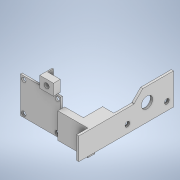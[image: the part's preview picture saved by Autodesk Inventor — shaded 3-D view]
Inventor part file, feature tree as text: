
AUTODESK INVENTOR PART (.ipt)
format: ipt  version: 2020.2 (Build 242310000, 310)  size: 344,576 bytes
history: native  units: mm
features: sketch x17, extrude x14, hole x4, projected_geometry x2
ambient origin geometry x8: Origin, YZ Plane, XZ Plane, XY Plane, X Axis, Y Axis, Z Axis, Center Point
bodies: Body1 (feature_tree)
feature tree (37):
  extrude  "Extrusion7"  Depth=6.08mm
  hole  "Hole4"  [1 undecoded]
  sketch  "Sketch16"  dims[d70=12.16mm d71=10.0mm]
  extrude  "Extrusion8"  Depth=10.0mm
  hole  "Hole5"  [1 undecoded]
  extrude  "Extrusion9"  Depth=32.05mm
  extrude  "Extrusion10"  Depth=32.05mm
  extrude  "Extrusion11"  Depth=3.0mm
  hole  "Hole6"  [1 undecoded]
  hole  "Hole7"  [1 undecoded]
  extrude  "Extrusion13"  Depth=26.05mm
  extrude  "Extrusion14"  Depth=4.0mm TaperAngle=0.0deg
  extrude  "Extrusion15"  Depth=10.0mm
  extrude  "Extrusion16"  TaperAngle=90.0deg  [1 undecoded]
  extrude  "Extrusion17"  TaperAngle=90.0deg  [1 undecoded]
  extrude  "Extrusion18"  Depth=2.5mm TaperAngle=0.0deg
  extrude  "Extrusion19"  Depth=5.0mm
  extrude  "Extrusion20"  TaperAngle=90.0deg  [1 undecoded]
  extrude  "Extrusion21"  Depth=5.0mm
  sketch  "Sketch14"  dims[d66=6.08mm d67=6.08mm]
  sketch  "Sketch15"  dims[d68=5.0mm d69=90.0deg]
  sketch  "Sketch17"  dims[d72=2.0mm d73=0.0mm]
  projected_geometry  "Projected Loop2"
  sketch  "Sketch18"  dims[d74=4.5mm d75=6.0mm d76=9.4mm d77=2.0mm d78=90.0deg d79=8.0mm d80=20.594885mm d81=10.0mm]
  projected_geometry  "Projected Loop3"
  sketch  "Sketch19"  dims[d82=35.7mm d83=32.05mm]
  sketch  "Sketch21"  dims[d84=35.7mm d85=32.05mm]
  sketch  "Sketch22"  dims[d86=3.0mm d87=3.0mm]
  sketch  "Sketch23"  dims[d88=29.7mm d89=26.05mm]
  sketch  "Sketch24"  dims[d90=3.0mm d91=3.0mm]
  sketch  "Sketch25"  dims[d92=29.7mm d93=26.05mm]
  sketch  "Sketch26"  dims[d94=1.5mm d95=0.0mm]
  sketch  "Sketch27"  dims[d96=3.9mm d97=6.0mm d98=8.2mm d99=2.0mm d100=90.0deg d101=8.0mm d102=20.594885mm d103=4.0mm d104=0.0mm]
  sketch  "Sketch28"  dims[d105=30.0mm d106=0.0mm d107=10.0mm]
  sketch  "Sketch29"  dims[d108=50.0mm d109=90.0deg]
  sketch  "Sketch30"  dims[d110=45.0mm d111=90.0deg]
  sketch  "Sketch31"  dims[d112=25.0mm d113=2.5mm d114=0.0mm d118=14.05mm d119=90.0deg d120=6.713mm d121=90.0deg d122=10.0mm d123=6.0mm d124=8.2mm d125=2.0mm d126=90.0deg d127=8.0mm d128=20.594885mm d129=8.0mm d130=90.0deg d131=17.5mm d132=90.0deg d133=35.0mm d134=4.2mm d135=6.0mm d136=8.2mm d137=2.0mm d138=90.0deg d139=8.0mm d140=20.594885mm d141=9.0mm d142=90.0deg d145=35.0mm d146=0.0mm d147=11.0mm d148=135.0deg d149=20.0mm d150=35.0mm d151=0.0mm d152=20.0mm d153=90.0deg d154=90.0deg d155=11.45mm d156=4.669mm d157=90.0deg d158=8.0mm d159=17.5mm d160=35.0mm d161=4.2mm d162=4.2mm d163=10.0mm d164=2.0mm d165=0.0mm d166=2.0mm d167=0.0mm d168=35.0mm d169=2.0mm d170=10.0mm d171=0.0mm d172=10.0mm d173=40.0mm d174=10.0mm d175=0.0mm d176=10.0mm d177=0.0mm d178=10.0mm d179=0.0mm d180=12.16mm d181=10.0mm d182=0.0mm d183=16.0mm d184=10.0mm d185=0.0mm d186=1.0mm d187=5.0mm d188=0.0mm]
note: 7 required parameter values undecoded (feature->parameter linkage not recoverable at this tier; creation-order binding heuristic only, values carry confidence <= 0.55)
